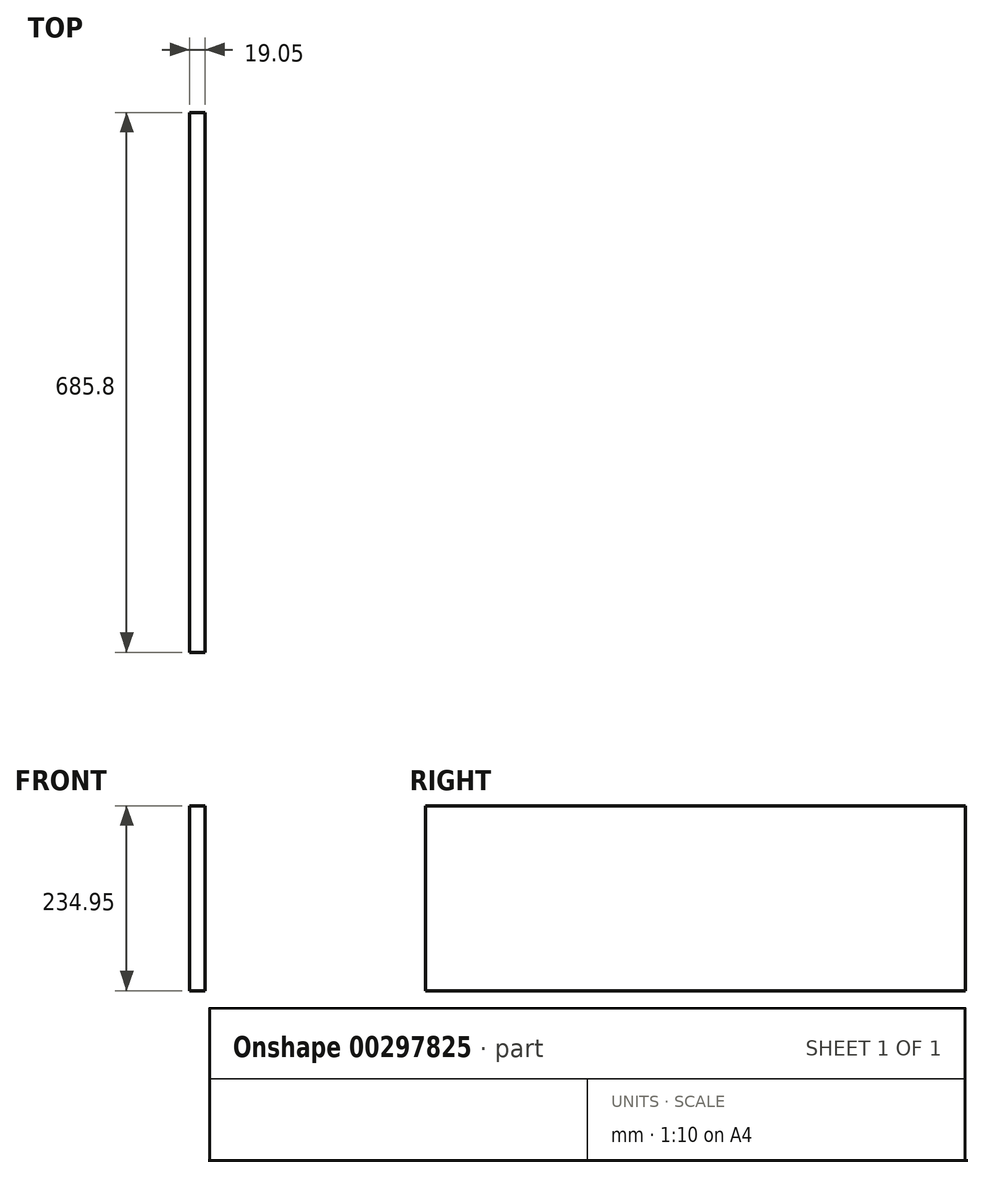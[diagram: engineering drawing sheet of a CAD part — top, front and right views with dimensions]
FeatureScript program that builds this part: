
annotation { "Feature Type Name" : "Feature", "Feature Type Description" : "" }
export const myFeature = defineFeature(function(context is Context, id is Id, definition is map)
    precondition{}
    {
        {
            var Q0;
            Q0=qCreatedBy(makeId("Right.planeOp"),FACE);
            var sketch = newSketch(context, id + "F0", { "sketchPlane" : qUnion([Q0])});
            skLineSegment(sketch, "E0.bottom", {"start": v(3.3, 0) * mm, "end": v(689.1, 0) * mm});
            skLineSegment(sketch, "E0.top", {"start": v(3.3, 234.95) * mm, "end": v(689.1, 234.95) * mm});
            skLineSegment(sketch, "E0.left", {"start": v(3.3, 0) * mm, "end": v(3.3, 234.95) * mm});
            skLineSegment(sketch, "E0.right", {"start": v(689.1, 0) * mm, "end": v(689.1, 234.95) * mm});
            skSolve(sketch);
        }
        {
            var Q0;
            Q0=makeQuery(id+"F0.imprint","IMPRINT",FACE,{"disambiguationData":[TD([[makeQuery(id+"F0.imprint","IMPRINT",EDGE,{"derivedFrom":sQuery(id+"F0.wireOp",EDGE,"E0.bottom")}),1.0]])]});
            extrude(context, id + "F1", {"entities" : qUnion([Q0]), "depth" : 19.05 * mm});
        }
    });
